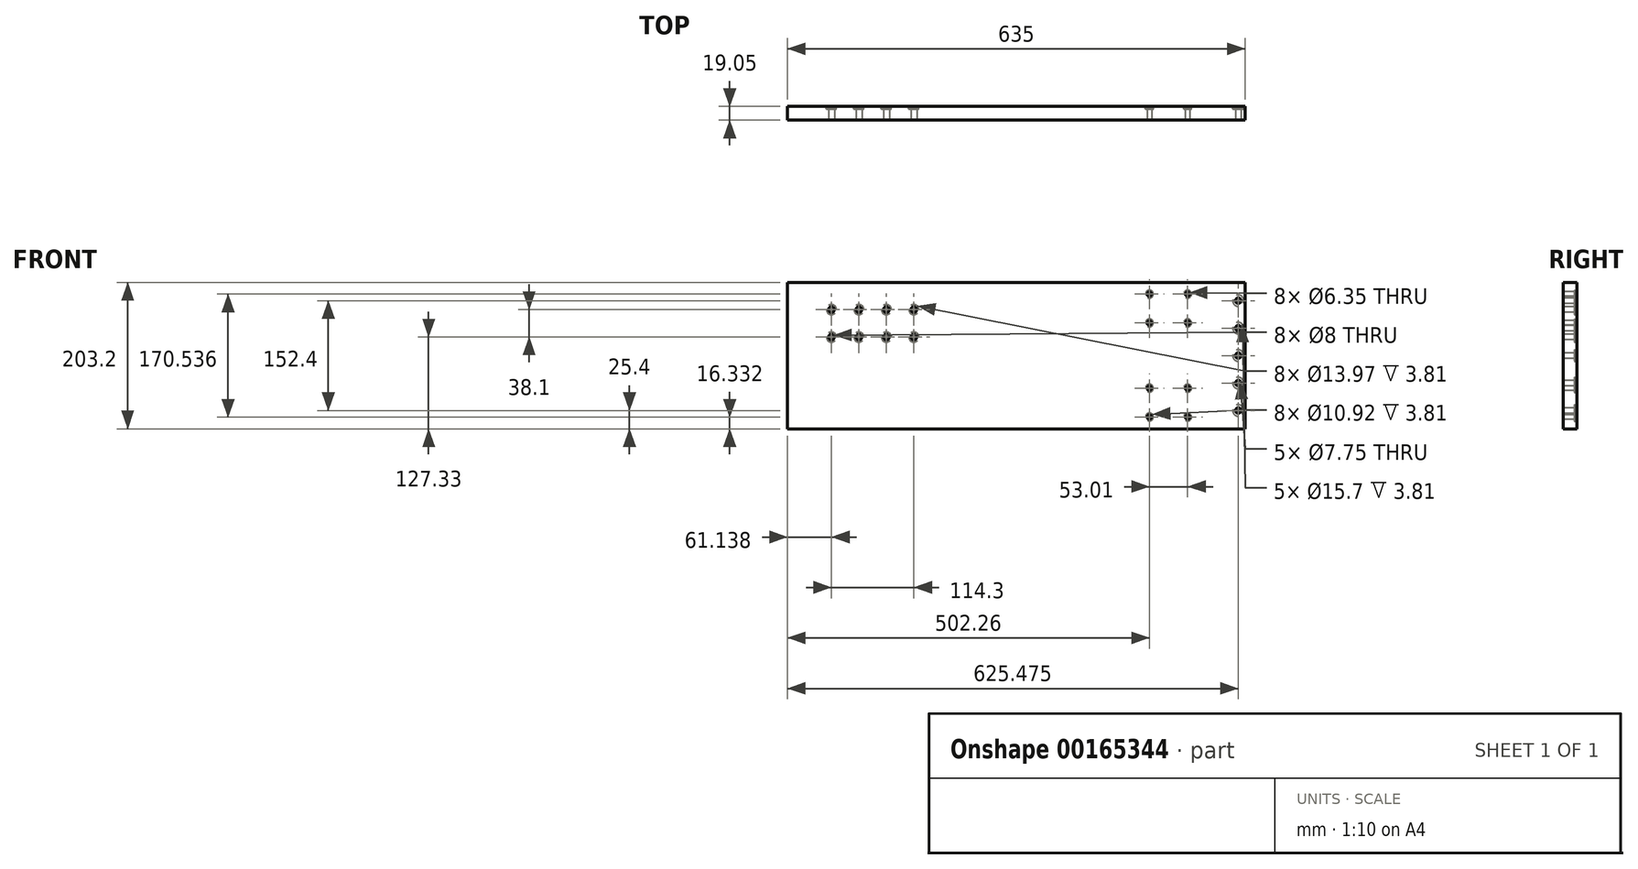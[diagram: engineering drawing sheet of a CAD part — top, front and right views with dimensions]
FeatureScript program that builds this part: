
annotation { "Feature Type Name" : "Feature", "Feature Type Description" : "" }
export const myFeature = defineFeature(function(context is Context, id is Id, definition is map)
    precondition{}
    {
        {
            var Q0;
            Q0=qCreatedBy(makeId("Front.planeOp"),FACE);
            var sketch = newSketch(context, id + "F0", { "sketchPlane" : qUnion([Q0])});
            skLineSegment(sketch, "E0.rect.bottom", {"start": v(317.5, 101.6) * mm, "end": v(-317.5, 101.6) * mm});
            skLineSegment(sketch, "E0.rect.top", {"start": v(317.5, -101.6) * mm, "end": v(-317.5, -101.6) * mm});
            skLineSegment(sketch, "E0.rect.left", {"start": v(317.5, 101.6) * mm, "end": v(317.5, -101.6) * mm});
            skLineSegment(sketch, "E0.rect.right", {"start": v(-317.5, 101.6) * mm, "end": v(-317.5, -101.6) * mm});
            skPoint(sketch, "E0.rect.middle", {"position": v(0, 0) * mm});
            skSolve(sketch);
        }
        {
            var Q0;
            Q0=qSketchRegion(id+"F0",true);
            extrude(context, id + "F1", {"entities" : qUnion([Q0]), "depth" : 19.05 * mm});
        }
        {
            var Q0;
            Q0=makeQuery(id+"F1.opExtrude","CAP_FACE",FACE,{"disambiguationData":[OSD([sQuery(id+"F0.wireOp",EDGE,"E0.rect.bottom"),sQuery(id+"F0.wireOp",EDGE,"E0.rect.top"),sQuery(id+"F0.wireOp",EDGE,"E0.rect.left"),sQuery(id+"F0.wireOp",EDGE,"E0.rect.right")])],"isStart":false});
            var sketch = newSketch(context, id + "F2", { "sketchPlane" : qUnion([Q0])});
            skLineSegment(sketch, "E1", {"start": v(-317.5, 25.73) * mm, "end": v(317.5, 25.73) * mm, "construction": true});
            skLineSegment(sketch, "E2", {"start": v(-256.36, 101.6) * mm, "end": v(-256.36, -101.6) * mm, "construction": true});
            skLineSegment(sketch, "E3", {"start": v(-317.5, 63.83) * mm, "end": v(317.5, 63.83) * mm, "construction": true});
            skLineSegment(sketch, "E4", {"start": v(-218.26, 101.6) * mm, "end": v(-218.26, -101.6) * mm, "construction": true});
            skLineSegment(sketch, "E5", {"start": v(-180.16, 101.6) * mm, "end": v(-180.16, -101.6) * mm, "construction": true});
            skLineSegment(sketch, "E6", {"start": v(-142.06, 101.6) * mm, "end": v(-142.06, -101.6) * mm, "construction": true});
            skCircle(sketch, "E7", {"center": v(-256.36, 63.83) * mm, "radius": 4 * mm});
            skCircle(sketch, "E8", {"center": v(-218.26, 63.83) * mm, "radius": 4 * mm});
            skCircle(sketch, "E9", {"center": v(-180.16, 63.83) * mm, "radius": 4 * mm});
            skCircle(sketch, "E10", {"center": v(-142.06, 63.83) * mm, "radius": 4 * mm});
            skCircle(sketch, "E11", {"center": v(-142.06, 25.73) * mm, "radius": 4 * mm});
            skCircle(sketch, "E12", {"center": v(-180.16, 25.73) * mm, "radius": 4 * mm});
            skCircle(sketch, "E13", {"center": v(-218.26, 25.73) * mm, "radius": 4 * mm});
            skCircle(sketch, "E14", {"center": v(-256.36, 25.73) * mm, "radius": 4 * mm});
            skSolve(sketch);
        }
        {
            var Q0;
            Q0=qSketchRegion(id+"F2",true);
            extrude(context, id + "F3", {"entities" : qUnion([Q0]), "operationType" : NewBodyOperationType.REMOVE, "endBound" : BoundingType.THROUGH_ALL, "oppositeDirection" : true, "depth" : 25.4 * mm});
        }
        {
            var Q0;
            Q0=makeQuery(id+"F1.opExtrude","CAP_FACE",FACE,{"disambiguationData":[OSD([sQuery(id+"F0.wireOp",EDGE,"E0.rect.bottom"),sQuery(id+"F0.wireOp",EDGE,"E0.rect.top"),sQuery(id+"F0.wireOp",EDGE,"E0.rect.left"),sQuery(id+"F0.wireOp",EDGE,"E0.rect.right")])],"isStart":false});
            var sketch = newSketch(context, id + "F4", { "sketchPlane" : qUnion([Q0])});
            skLineSegment(sketch, "E15", {"start": v(237.77, 101.6) * mm, "end": v(237.77, -101.6) * mm, "construction": true});
            skLineSegment(sketch, "E16", {"start": v(184.76, 101.6) * mm, "end": v(184.76, -101.6) * mm, "construction": true});
            skLineSegment(sketch, "E17", {"start": v(317.5, 85.27) * mm, "end": v(-317.5, 85.27) * mm, "construction": true});
            skLineSegment(sketch, "E18", {"start": v(317.5, -85.27) * mm, "end": v(-317.5, -85.27) * mm, "construction": true});
            skLineSegment(sketch, "E19", {"start": v(317.5, 45.26) * mm, "end": v(-317.5, 45.26) * mm, "construction": true});
            skLineSegment(sketch, "E20", {"start": v(317.5, -45.26) * mm, "end": v(-317.5, -45.26) * mm, "construction": true});
            skCircle(sketch, "E21", {"center": v(184.76, 85.27) * mm, "radius": 3.18 * mm});
            skCircle(sketch, "E22", {"center": v(237.77, 85.27) * mm, "radius": 3.18 * mm});
            skCircle(sketch, "E23", {"center": v(184.76, 45.26) * mm, "radius": 3.18 * mm});
            skCircle(sketch, "E24", {"center": v(237.77, 45.26) * mm, "radius": 3.18 * mm});
            skCircle(sketch, "E25", {"center": v(184.76, -45.26) * mm, "radius": 3.18 * mm});
            skCircle(sketch, "E26", {"center": v(237.77, -45.26) * mm, "radius": 3.18 * mm});
            skCircle(sketch, "E27", {"center": v(184.76, -85.27) * mm, "radius": 3.18 * mm});
            skCircle(sketch, "E28", {"center": v(237.77, -85.27) * mm, "radius": 3.18 * mm});
            skSolve(sketch);
        }
        {
            var Q0;
            Q0=qSketchRegion(id+"F4",true);
            extrude(context, id + "F5", {"entities" : qUnion([Q0]), "operationType" : NewBodyOperationType.REMOVE, "endBound" : BoundingType.THROUGH_ALL, "oppositeDirection" : true, "depth" : 25.4 * mm});
        }
        {
            var Q0;
            Q0=makeQuery(id+"F1.opExtrude","CAP_FACE",FACE,{"disambiguationData":[OSD([sQuery(id+"F0.wireOp",EDGE,"E0.rect.bottom"),sQuery(id+"F0.wireOp",EDGE,"E0.rect.top"),sQuery(id+"F0.wireOp",EDGE,"E0.rect.left"),sQuery(id+"F0.wireOp",EDGE,"E0.rect.right")])],"isStart":false});
            var sketch = newSketch(context, id + "F6", { "sketchPlane" : qUnion([Q0])});
            skLineSegment(sketch, "E29", {"start": v(307.98, 101.6) * mm, "end": v(307.98, -101.6) * mm, "construction": true});
            skLineSegment(sketch, "E30", {"start": v(-317.5, 76.2) * mm, "end": v(317.5, 76.2) * mm, "construction": true});
            skLineSegment(sketch, "E31", {"start": v(-317.5, 38.1) * mm, "end": v(317.5, 38.1) * mm, "construction": true});
            skLineSegment(sketch, "E32", {"start": v(-317.5, -38.1) * mm, "end": v(317.5, -38.1) * mm, "construction": true});
            skLineSegment(sketch, "E33", {"start": v(-317.5, -76.2) * mm, "end": v(317.5, -76.2) * mm, "construction": true});
            skLineSegment(sketch, "E34", {"start": v(-317.5, 0) * mm, "end": v(317.5, 0) * mm, "construction": true});
            skCircle(sketch, "E35", {"center": v(307.98, 76.2) * mm, "radius": 3.87 * mm});
            skCircle(sketch, "E36", {"center": v(307.98, 38.1) * mm, "radius": 3.87 * mm});
            skCircle(sketch, "E37", {"center": v(307.98, 0) * mm, "radius": 3.87 * mm});
            skCircle(sketch, "E38", {"center": v(307.98, -38.1) * mm, "radius": 3.87 * mm});
            skCircle(sketch, "E39", {"center": v(307.98, -76.2) * mm, "radius": 3.87 * mm});
            skSolve(sketch);
        }
        {
            var Q0;
            Q0=qSketchRegion(id+"F6",true);
            extrude(context, id + "F7", {"entities" : qUnion([Q0]), "operationType" : NewBodyOperationType.REMOVE, "endBound" : BoundingType.THROUGH_ALL, "oppositeDirection" : true, "depth" : 25.4 * mm});
        }
        {
            var Q0;
            Q0=makeQuery(id+"F1.opExtrude","CAP_FACE",FACE,{"disambiguationData":[OSD([sQuery(id+"F0.wireOp",EDGE,"E0.rect.bottom"),sQuery(id+"F0.wireOp",EDGE,"E0.rect.top"),sQuery(id+"F0.wireOp",EDGE,"E0.rect.left"),sQuery(id+"F0.wireOp",EDGE,"E0.rect.right")])],"isStart":true});
            var sketch = newSketch(context, id + "F8", { "sketchPlane" : qUnion([Q0])});
            skCircle(sketch, "E40", {"center": v(142.06, 63.83) * mm, "radius": 6.99 * mm});
            skCircle(sketch, "E41", {"center": v(180.16, 63.83) * mm, "radius": 6.99 * mm});
            skCircle(sketch, "E42", {"center": v(218.26, 63.83) * mm, "radius": 6.99 * mm});
            skCircle(sketch, "E43", {"center": v(256.36, 63.83) * mm, "radius": 6.99 * mm});
            skCircle(sketch, "E44", {"center": v(142.06, 25.73) * mm, "radius": 6.99 * mm});
            skCircle(sketch, "E45", {"center": v(180.16, 25.73) * mm, "radius": 6.99 * mm});
            skCircle(sketch, "E46", {"center": v(218.26, 25.73) * mm, "radius": 6.99 * mm});
            skCircle(sketch, "E47", {"center": v(256.36, 25.73) * mm, "radius": 6.99 * mm});
            skSolve(sketch);
        }
        {
            var Q0;
            Q0 = qSketchRegion(id + "F8", true);
            extrude(context, id + "F9", {"entities" : qUnion([Q0]), "operationType" : NewBodyOperationType.REMOVE, "oppositeDirection" : true, "depth" : 3.8 * mm});
        }
        {
            var Q0;
            Q0=makeQuery(id+"F1.opExtrude","CAP_FACE",FACE,{"disambiguationData":[OSD([sQuery(id+"F0.wireOp",EDGE,"E0.rect.bottom"),sQuery(id+"F0.wireOp",EDGE,"E0.rect.top"),sQuery(id+"F0.wireOp",EDGE,"E0.rect.left"),sQuery(id+"F0.wireOp",EDGE,"E0.rect.right")])],"isStart":true});
            var sketch = newSketch(context, id + "F10", { "sketchPlane" : qUnion([Q0])});
            skCircle(sketch, "E48", {"center": v(-307.98, 76.2) * mm, "radius": 7.85 * mm});
            skCircle(sketch, "E49", {"center": v(-307.98, 38.1) * mm, "radius": 7.85 * mm});
            skCircle(sketch, "E50", {"center": v(-307.98, 0) * mm, "radius": 7.85 * mm});
            skCircle(sketch, "E51", {"center": v(-307.98, -38.1) * mm, "radius": 7.85 * mm});
            skCircle(sketch, "E52", {"center": v(-307.98, -76.2) * mm, "radius": 7.85 * mm});
            skSolve(sketch);
        }
        {
            var Q0;
            Q0 = qSketchRegion(id + "F10", true);
            extrude(context, id + "F11", {"entities" : qUnion([Q0]), "operationType" : NewBodyOperationType.REMOVE, "oppositeDirection" : true, "depth" : 3.8 * mm});
        }
        {
            var Q0;
            Q0=makeQuery(id+"F1.opExtrude","CAP_FACE",FACE,{"disambiguationData":[OSD([sQuery(id+"F0.wireOp",EDGE,"E0.rect.bottom"),sQuery(id+"F0.wireOp",EDGE,"E0.rect.top"),sQuery(id+"F0.wireOp",EDGE,"E0.rect.left"),sQuery(id+"F0.wireOp",EDGE,"E0.rect.right")])],"isStart":true});
            var sketch = newSketch(context, id + "F12", { "sketchPlane" : qUnion([Q0])});
            skCircle(sketch, "E53", {"center": v(-237.77, 85.27) * mm, "radius": 5.46 * mm});
            skCircle(sketch, "E54", {"center": v(-184.76, 85.27) * mm, "radius": 5.46 * mm});
            skCircle(sketch, "E55", {"center": v(-184.76, 45.26) * mm, "radius": 5.46 * mm});
            skCircle(sketch, "E56", {"center": v(-237.77, 45.26) * mm, "radius": 5.46 * mm});
            skCircle(sketch, "E57", {"center": v(-237.77, -45.26) * mm, "radius": 5.46 * mm});
            skCircle(sketch, "E58", {"center": v(-184.76, -45.26) * mm, "radius": 5.46 * mm});
            skCircle(sketch, "E59", {"center": v(-184.76, -85.27) * mm, "radius": 5.46 * mm});
            skCircle(sketch, "E60", {"center": v(-237.77, -85.27) * mm, "radius": 5.46 * mm});
            skSolve(sketch);
        }
        {
            var Q0;
            Q0 = qSketchRegion(id + "F12", true);
            extrude(context, id + "F13", {"entities" : qUnion([Q0]), "operationType" : NewBodyOperationType.REMOVE, "oppositeDirection" : true, "depth" : 3.8 * mm});
        }
    });
